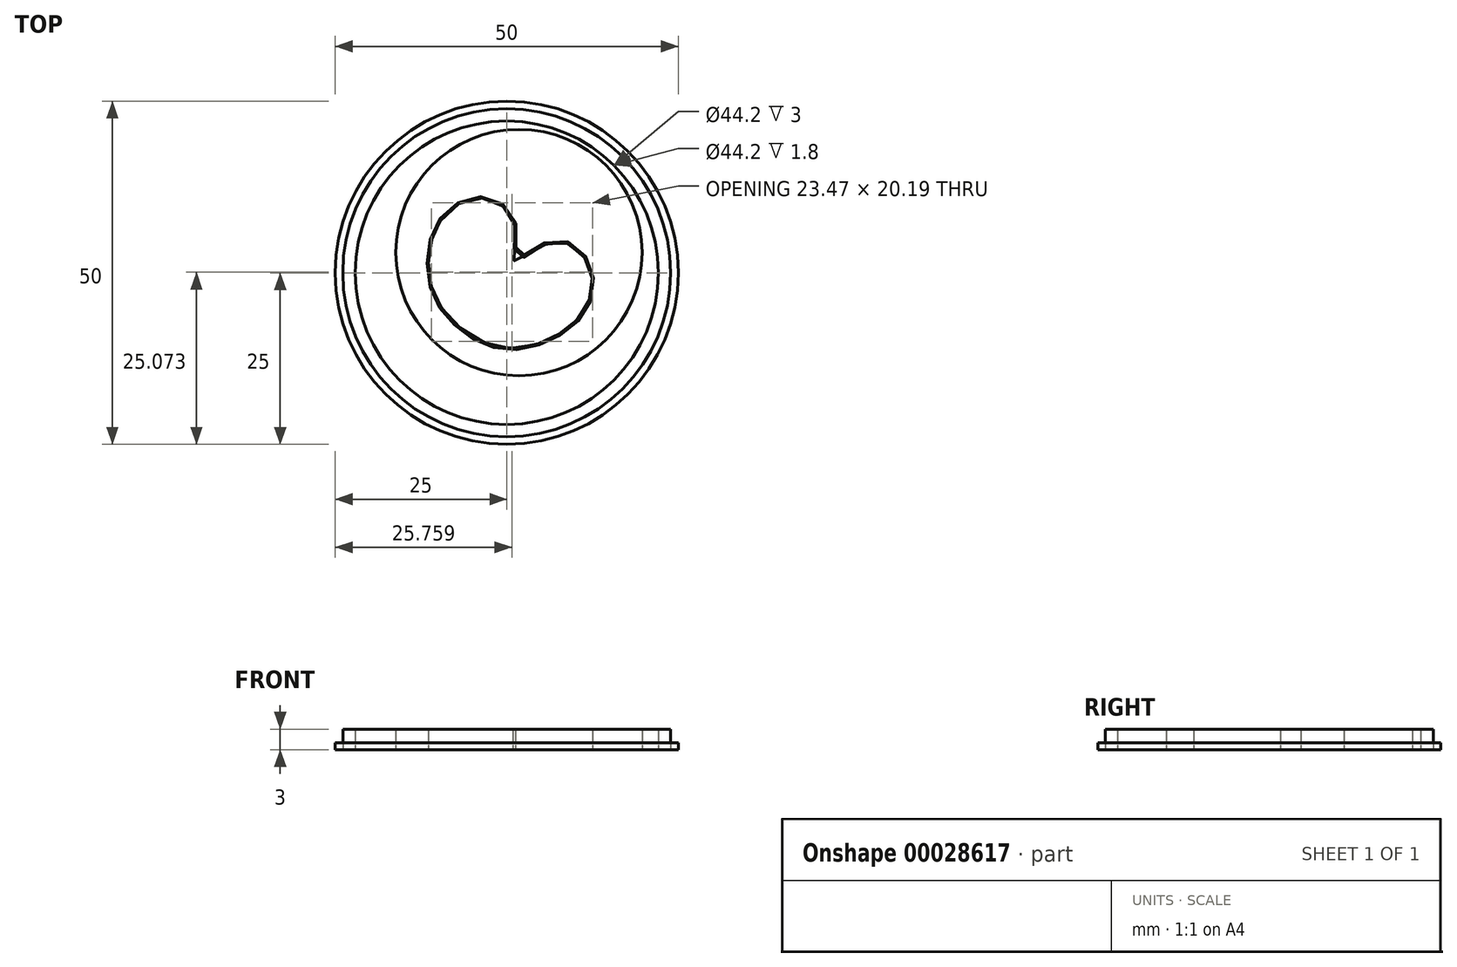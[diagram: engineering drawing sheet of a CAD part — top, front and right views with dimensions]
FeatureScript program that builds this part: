
annotation { "Feature Type Name" : "Feature", "Feature Type Description" : "" }
export const myFeature = defineFeature(function(context is Context, id is Id, definition is map)
    precondition{}
    {
        {
            var Q0;
            Q0=qCreatedBy(makeId("Top.planeOp"),FACE);
            var sketch = newSketch(context, id + "F0", { "sketchPlane" : qUnion([Q0])});
            skCircle(sketch, "E0", {"center": v(0, 0) * mm, "radius": 25 * mm});
            skCircle(sketch, "E1", {"center": v(0, 0) * mm, "radius": 23.9 * mm});
            skCircle(sketch, "E2", {"center": v(0, 0) * mm, "radius": 22.1 * mm});
            skCircle(sketch, "E3", {"center": v(1.78, 2.94) * mm, "radius": 17.95 * mm});
            skPoint(sketch, "E4", {"position": v(0, 25) * mm});
            skPoint(sketch, "E5", {"position": v(0, 20.8) * mm});
            skPoint(sketch, "E6", {"position": v(-15.93, 0) * mm});
            skPoint(sketch, "E7", {"position": v(-25, 0) * mm});
            skLineSegment(sketch, "E8", {"start": v(0.34, 31.79) * mm, "end": v(0.34, -39.78) * mm, "construction": true});
            skPoint(sketch, "E9", {"position": v(0.34, 0) * mm});
            skPoint(sketch, "E10", {"position": v(-3.9, 10.89) * mm});
            skPoint(sketch, "E11", {"position": v(12.51, -1.48) * mm});
            skPoint(sketch, "E12", {"position": v(0.65, -11.01) * mm});
            skPoint(sketch, "E13", {"position": v(-11.43, 1.18) * mm});
            skFitSpline(sketch, "E14", {"points": [v(-10.98, -2) * mm, v(-11.37, -0.01) * mm, v(-11.4, 1.98) * mm, v(-11.15, 3.98) * mm, v(-10.56, 5.9) * mm, v(-10.17, 6.73) * mm, v(-9.73, 7.55) * mm, v(-8.59, 8.96) * mm, v(-6.33, 10.35) * mm, v(-4.5, 10.86) * mm, v(-2.83, 10.77) * mm, v(-1.23, 10.17) * mm, v(0.23, 9.1) * mm, v(0.95, 7.82) * mm, v(1.27, 6.13) * mm, v(1.18, 4) * mm, v(0.99, 2.8) * mm, v(0.86, 2.24) * mm, v(0.93, 1.94) * mm, v(1.1, 1.73) * mm, v(1.55, 1.62) * mm, v(1.95, 1.8) * mm, v(3.45, 2.98) * mm, v(4.68, 3.75) * mm, v(6.04, 4.35) * mm, v(7.5, 4.61) * mm, v(8.89, 4.32) * mm, v(10.24, 3.45) * mm, v(11.54, 2.03) * mm, v(12.21, 0.64) * mm, v(12.5, -1.02) * mm, v(12.48, -2.05) * mm, v(12.07, -3.85) * mm, v(11.28, -5.48) * mm, v(10.26, -6.9) * mm, v(8.96, -8.07) * mm, v(7.48, -9.04) * mm, v(5.93, -9.85) * mm, v(2.94, -10.82) * mm, v(0.92, -11) * mm, v(-1.1, -10.87) * mm, v(-3.45, -10.13) * mm, v(-5.61, -8.95) * mm, v(-8.2, -6.79) * mm, v(-9.57, -5.06) * mm, v(-10.6, -3.07) * mm, v(-10.98, -2) * mm]});
            skLineSegment(sketch, "E15", {"start": v(-11.43, 18.63) * mm, "end": v(-11.43, -20.08) * mm, "construction": true});
            skLineSegment(sketch, "E16", {"start": v(-26.76, 10.89) * mm, "end": v(26.59, 10.89) * mm, "construction": true});
            skLineSegment(sketch, "E17", {"start": v(12.51, 19.74) * mm, "end": v(12.51, -18.58) * mm, "construction": true});
            skLineSegment(sketch, "E18", {"start": v(26.08, -11.01) * mm, "end": v(-24.25, -11.01) * mm, "construction": true});
            skSolve(sketch);
        }
        {
            var Q0;
            Q0=makeQuery(id+"F0.imprint","IMPRINT",FACE,{"disambiguationData":[TD([[makeQuery(id+"F0.imprint","IMPRINT",EDGE,{"derivedFrom":sQuery(id+"F0.wireOp",EDGE,"E0")}),1.0]])]});
            extrude(context, id + "F1", {"entities" : qUnion([Q0]), "depth" : 1 * mm});
        }
        {
            var Q0;
            Q0=makeQuery(id+"F0.imprint","IMPRINT",FACE,{"disambiguationData":[TD([[makeQuery(id+"F0.imprint","IMPRINT",EDGE,{"derivedFrom":sQuery(id+"F0.wireOp",EDGE,"E1")}),1.0]])]});
            extrude(context, id + "F2", {"entities" : qUnion([Q0]), "operationType" : NewBodyOperationType.ADD, "depth" : 3 * mm});
        }
        {
            var Q0;
            Q0=makeQuery(id+"F0.imprint","IMPRINT",FACE,{"disambiguationData":[TD([[makeQuery(id+"F0.imprint","IMPRINT",EDGE,{"derivedFrom":sQuery(id+"F0.wireOp",EDGE,"E2")}),1.0]])]});
            extrude(context, id + "F3", {"entities" : qUnion([Q0]), "operationType" : NewBodyOperationType.ADD, "depth" : 1 * mm});
        }
        {
            var Q0;
            Q0=makeQuery(id+"F0.imprint","IMPRINT",FACE,{"disambiguationData":[TD([[makeQuery(id+"F0.imprint","IMPRINT",EDGE,{"derivedFrom":sQuery(id+"F0.wireOp",EDGE,"E3")}),1.0]])]});
            extrude(context, id + "F4", {"entities" : qUnion([Q0]), "operationType" : NewBodyOperationType.ADD, "depth" : 3 * mm});
        }
        {
            var Q0;
            Q0=makeQuery(id+"F0.imprint","IMPRINT",FACE,{"disambiguationData":[TD([[makeQuery(id+"F0.imprint","IMPRINT",EDGE,{"derivedFrom":sQuery(id+"F0.wireOp",EDGE,"E14")}),-1.0]])]});
            extrude(context, id + "F5", {"entities" : qUnion([Q0]), "operationType" : NewBodyOperationType.ADD, "depth" : 1 * mm});
        }
        {
            var Q0;
            Q0=makeQuery(id+"F2.opExtrude","CAP_EDGE",EDGE,{"disambiguationData":[OSD([sQuery(id+"F0.wireOp",EDGE,"E1")])],"isStart":false});
            var Q1;
            Q1=makeQuery(id+"F2.opExtrude","CAP_EDGE",EDGE,{"disambiguationData":[OSD([sQuery(id+"F0.wireOp",EDGE,"E2")])],"isStart":false});
            var Q2;
            Q2=makeQuery(id+"F4.opExtrude","CAP_EDGE",EDGE,{"disambiguationData":[OSD([sQuery(id+"F0.wireOp",EDGE,"E3")])],"isStart":false});
            var Q3;
            Q3=makeQuery(id+"F4.opExtrude","CAP_EDGE",EDGE,{"disambiguationData":[OSD([sQuery(id+"F0.wireOp",EDGE,"E14")])],"isStart":false});
            fillet(context, id + "F6", {"entities" : qUnion([Q0, Q1, Q2, Q3]), "radius" : .2 * mm, "tangentPropagation" : true, "allowEdgeOverflow" : false});
        }
        {
            var Q0;
            Q0=makeQuery(id+"F0.imprint","IMPRINT",FACE,{"disambiguationData":[TD([[makeQuery(id+"F0.imprint","IMPRINT",EDGE,{"derivedFrom":sQuery(id+"F0.wireOp",EDGE,"E3")}),1.0]])]});
            var Q1;
            Q1=makeQuery(id+"F0.imprint","IMPRINT",FACE,{"disambiguationData":[TD([[makeQuery(id+"F0.imprint","IMPRINT",EDGE,{"derivedFrom":sQuery(id+"F0.wireOp",EDGE,"E1")}),1.0]])]});
            extrude(context, id + "F7", {"entities" : qUnion([Q0, Q1]), "depth" : 3 * mm});
        }
    });
